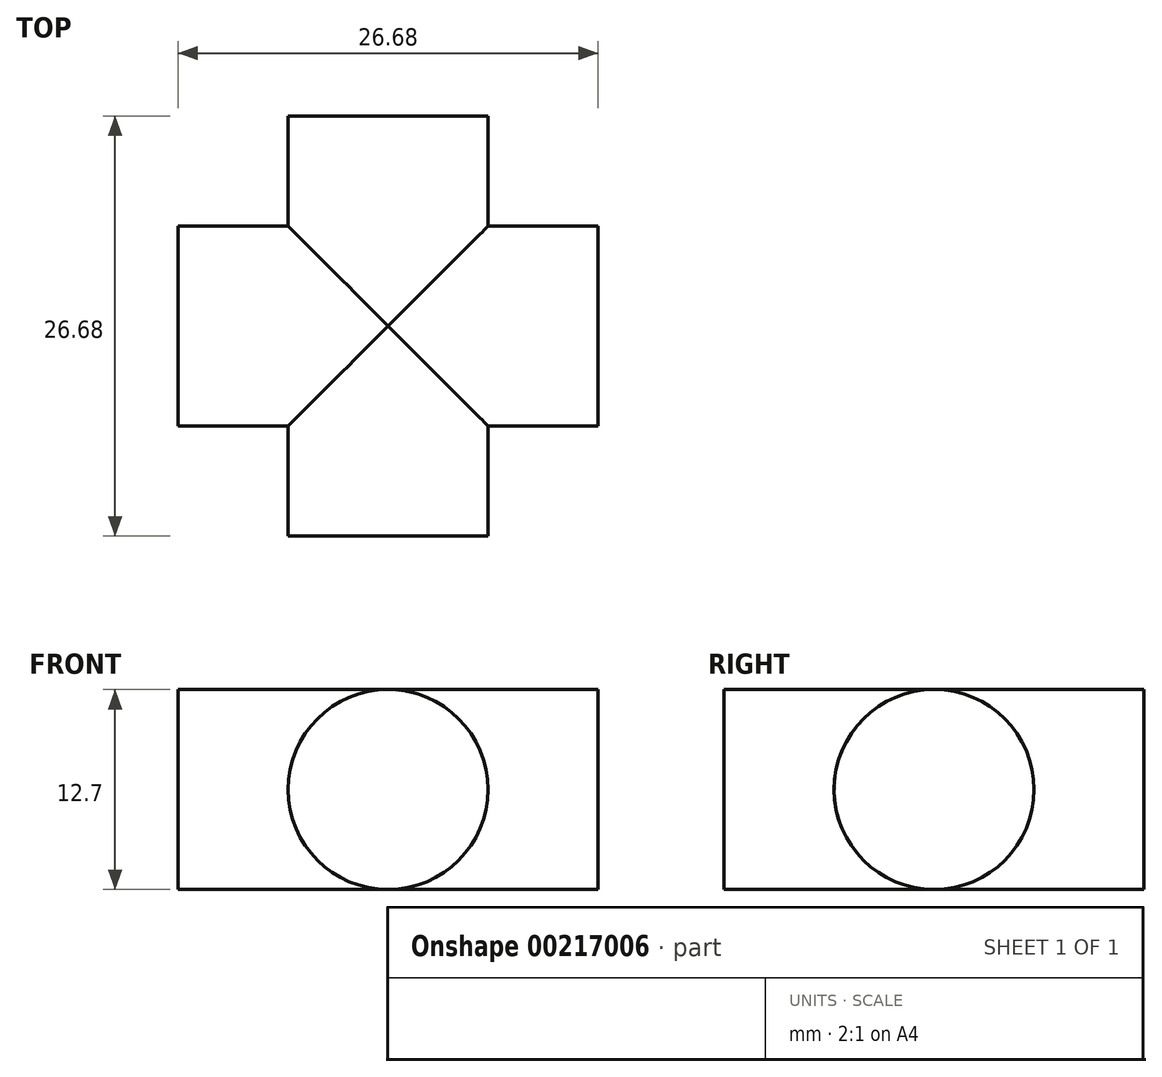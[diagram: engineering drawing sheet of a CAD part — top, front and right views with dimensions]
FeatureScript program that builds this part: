
annotation { "Feature Type Name" : "Feature", "Feature Type Description" : "" }
export const myFeature = defineFeature(function(context is Context, id is Id, definition is map)
    precondition{}
    {
        {
            var Q0;
            Q0=qCreatedBy(makeId("Front.planeOp"),FACE);
            var sketch = newSketch(context, id + "F0", { "sketchPlane" : qUnion([Q0])});
            skCircle(sketch, "E0", {"center": v(0, 0) * mm, "radius": 6.35 * mm});
            skSolve(sketch);
        }
        {
            var Q0;
            Q0=qCreatedBy(makeId("Right.planeOp"),FACE);
            var sketch = newSketch(context, id + "F1", { "sketchPlane" : qUnion([Q0])});
            skCircle(sketch, "E1", {"center": v(0, 0) * mm, "radius": 6.35 * mm});
            skSolve(sketch);
        }
        {
            var Q0;
            Q0=makeQuery(id+"F0.imprint","IMPRINT",FACE,{"disambiguationData":[TD([[makeQuery(id+"F0.imprint","IMPRINT",EDGE,{"derivedFrom":sQuery(id+"F0.wireOp",EDGE,"E0")}),1.0]])]});
            extrude(context, id + "F2", {"entities" : qUnion([Q0]), "depth" : 26.67 * mm, "symmetric" : true});
        }
        {
            var Q0;
            Q0=makeQuery(id+"F1.imprint","IMPRINT",FACE,{"disambiguationData":[TD([[makeQuery(id+"F1.imprint","IMPRINT",EDGE,{"derivedFrom":sQuery(id+"F1.wireOp",EDGE,"E1")}),1.0]])]});
            extrude(context, id + "F3", {"entities" : qUnion([Q0]), "operationType" : NewBodyOperationType.ADD, "depth" : 26.67 * mm, "symmetric" : true});
        }
    });
